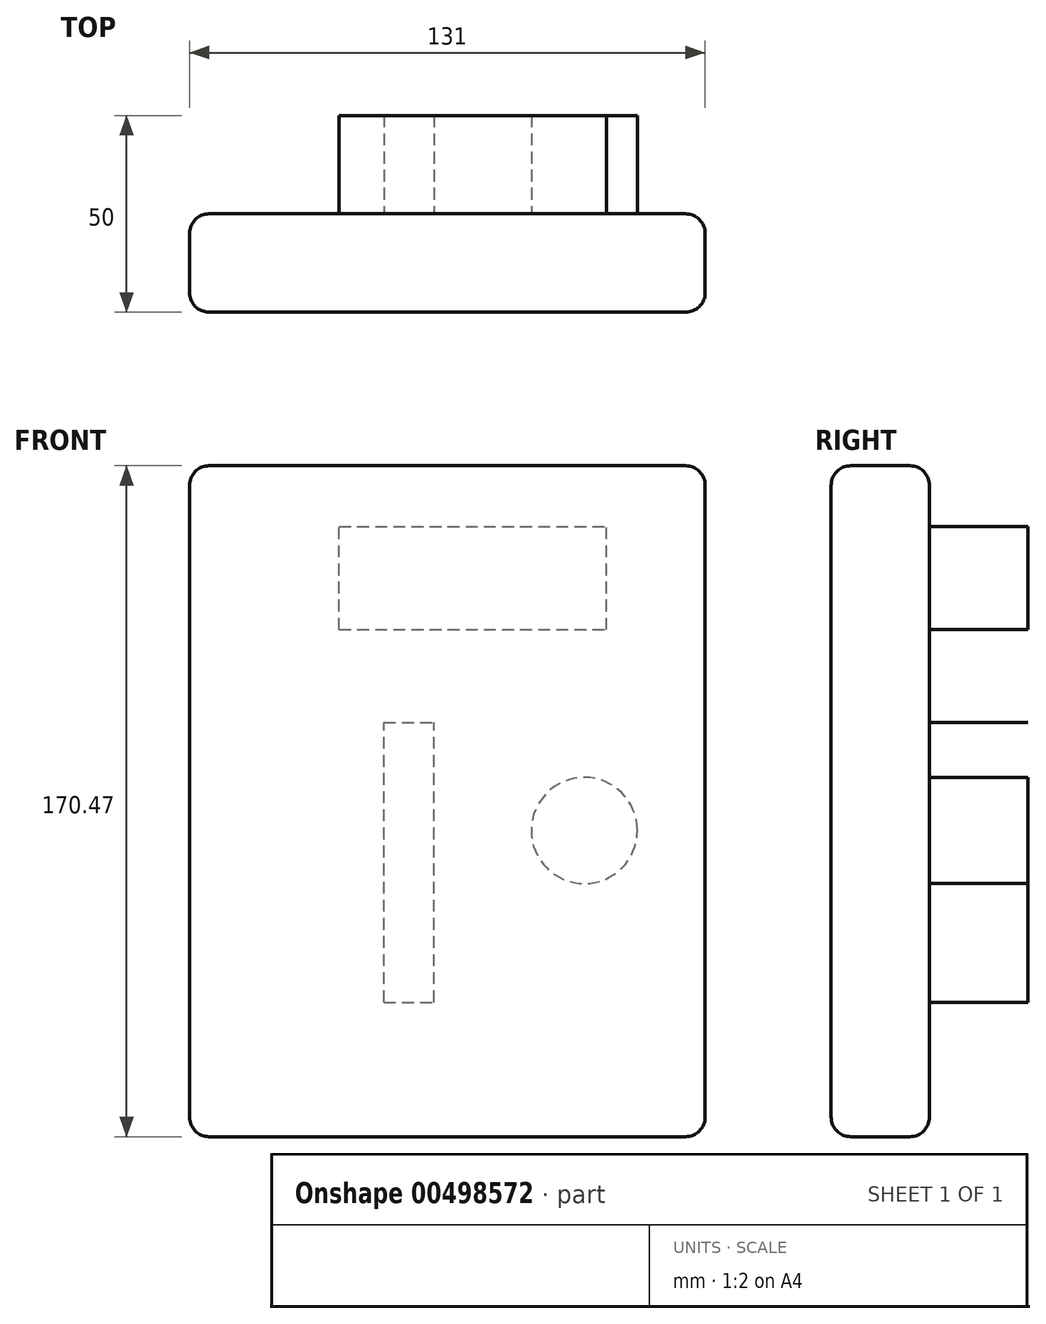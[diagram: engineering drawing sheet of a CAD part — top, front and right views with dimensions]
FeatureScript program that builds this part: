
annotation { "Feature Type Name" : "Feature", "Feature Type Description" : "" }
export const myFeature = defineFeature(function(context is Context, id is Id, definition is map)
    precondition{}
    {
        {
            var Q0;
            Q0=qCreatedBy(makeId("Front.planeOp"),FACE);
            var sketch = newSketch(context, id + "F0", { "sketchPlane" : qUnion([Q0])});
            skLineSegment(sketch, "E0.bottom", {"start": v(-95.11, 51.96) * mm, "end": v(35.89, 51.96) * mm});
            skLineSegment(sketch, "E0.top", {"start": v(-95.11, -118.51) * mm, "end": v(35.89, -118.51) * mm});
            skLineSegment(sketch, "E0.left", {"start": v(-95.11, 51.96) * mm, "end": v(-95.11, -118.51) * mm});
            skLineSegment(sketch, "E0.right", {"start": v(35.89, 51.96) * mm, "end": v(35.89, -118.51) * mm});
            skSolve(sketch);
        }
        {
            var Q0;
            Q0=makeQuery(id+"F0.imprint","IMPRINT",FACE,{"disambiguationData":[TD([[makeQuery(id+"F0.imprint","IMPRINT",EDGE,{"derivedFrom":sQuery(id+"F0.wireOp",EDGE,"E0.bottom")}),-1.0]])]});
            extrude(context, id + "F1", {"entities" : qUnion([Q0]), "depth" : 25 * mm});
        }
        {
            var Q0;
            Q0=makeQuery(id+"F1.opExtrude","CAP_EDGE",EDGE,{"disambiguationData":[OSD([sQuery(id+"F0.wireOp",EDGE,"E0.left")])],"isStart":true});
            var Q1;
            Q1=makeQuery(id+"F1.opExtrude","CAP_EDGE",EDGE,{"disambiguationData":[OSD([sQuery(id+"F0.wireOp",EDGE,"E0.top")])],"isStart":true});
            var Q2;
            Q2=makeQuery(id+"F1.opExtrude","CAP_EDGE",EDGE,{"disambiguationData":[OSD([sQuery(id+"F0.wireOp",EDGE,"E0.right")])],"isStart":true});
            var Q3;
            Q3=makeQuery(id+"F1.opExtrude","CAP_EDGE",EDGE,{"disambiguationData":[OSD([sQuery(id+"F0.wireOp",EDGE,"E0.bottom")])],"isStart":true});
            var Q4;
            Q4=makeQuery(id+"F1.opExtrude","SWEPT_EDGE",EDGE,{"disambiguationData":[OSD([sQuery(id+"F0.wireOp",EDGE,"E0.bottom"),sQuery(id+"F0.wireOp",EDGE,"E0.left")])]});
            var Q5;
            Q5=makeQuery(id+"F1.opExtrude","CAP_EDGE",EDGE,{"disambiguationData":[OSD([sQuery(id+"F0.wireOp",EDGE,"E0.bottom")])],"isStart":false});
            var Q6;
            Q6=makeQuery(id+"F1.opExtrude","SWEPT_EDGE",EDGE,{"disambiguationData":[OSD([sQuery(id+"F0.wireOp",EDGE,"E0.bottom"),sQuery(id+"F0.wireOp",EDGE,"E0.right")])]});
            var Q7;
            Q7=makeQuery(id+"F1.opExtrude","CAP_EDGE",EDGE,{"disambiguationData":[OSD([sQuery(id+"F0.wireOp",EDGE,"E0.top")])],"isStart":false});
            var Q8;
            Q8=makeQuery(id+"F1.opExtrude","CAP_EDGE",EDGE,{"disambiguationData":[OSD([sQuery(id+"F0.wireOp",EDGE,"E0.left")])],"isStart":false});
            var Q9;
            Q9=makeQuery(id+"F1.opExtrude","CAP_EDGE",EDGE,{"disambiguationData":[OSD([sQuery(id+"F0.wireOp",EDGE,"E0.right")])],"isStart":false});
            var Q10;
            Q10=makeQuery(id+"F1.opExtrude","SWEPT_EDGE",EDGE,{"disambiguationData":[OSD([sQuery(id+"F0.wireOp",EDGE,"E0.top"),sQuery(id+"F0.wireOp",EDGE,"E0.right")])]});
            var Q11;
            Q11=makeQuery(id+"F1.opExtrude","SWEPT_EDGE",EDGE,{"disambiguationData":[OSD([sQuery(id+"F0.wireOp",EDGE,"E0.top"),sQuery(id+"F0.wireOp",EDGE,"E0.left")])]});
            fillet(context, id + "F2", {"entities" : qUnion([Q0, Q1, Q2, Q3, Q4, Q5, Q6, Q7, Q8, Q9, Q10, Q11]), "radius" : 5 * mm, "tangentPropagation" : true, "allowEdgeOverflow" : false});
        }
        {
            var Q0;
            Q0=makeQuery(id+"F1.opExtrude","CAP_FACE",FACE,{"disambiguationData":[OSD([sQuery(id+"F0.wireOp",EDGE,"E0.bottom"),sQuery(id+"F0.wireOp",EDGE,"E0.top"),sQuery(id+"F0.wireOp",EDGE,"E0.left"),sQuery(id+"F0.wireOp",EDGE,"E0.right")])],"isStart":true});
            var sketch = newSketch(context, id + "F3", { "sketchPlane" : qUnion([Q0])});
            skLineSegment(sketch, "E1.bottom", {"start": v(45.72, -84.34) * mm, "end": v(32.97, -84.34) * mm});
            skLineSegment(sketch, "E1.top", {"start": v(45.72, -13.28) * mm, "end": v(32.97, -13.28) * mm});
            skLineSegment(sketch, "E1.left", {"start": v(45.72, -84.34) * mm, "end": v(45.72, -13.28) * mm});
            skLineSegment(sketch, "E1.right", {"start": v(32.97, -84.34) * mm, "end": v(32.97, -13.28) * mm});
            skLineSegment(sketch, "E2.bottom", {"start": v(57.11, 10.31) * mm, "end": v(-10.85, 10.31) * mm});
            skLineSegment(sketch, "E2.top", {"start": v(57.11, 36.52) * mm, "end": v(-10.85, 36.52) * mm});
            skLineSegment(sketch, "E2.left", {"start": v(57.11, 10.31) * mm, "end": v(57.11, 36.52) * mm});
            skLineSegment(sketch, "E2.right", {"start": v(-10.85, 10.31) * mm, "end": v(-10.85, 36.52) * mm});
            skCircle(sketch, "E3", {"center": v(-5.2, -40.72) * mm, "radius": 13.48 * mm});
            skSolve(sketch);
        }
        {
            var Q0;
            Q0 = qSketchRegion(id + "F3", true);
            extrude(context, id + "F4", {"entities" : qUnion([Q0]), "depth" : 25 * mm});
        }
    });
